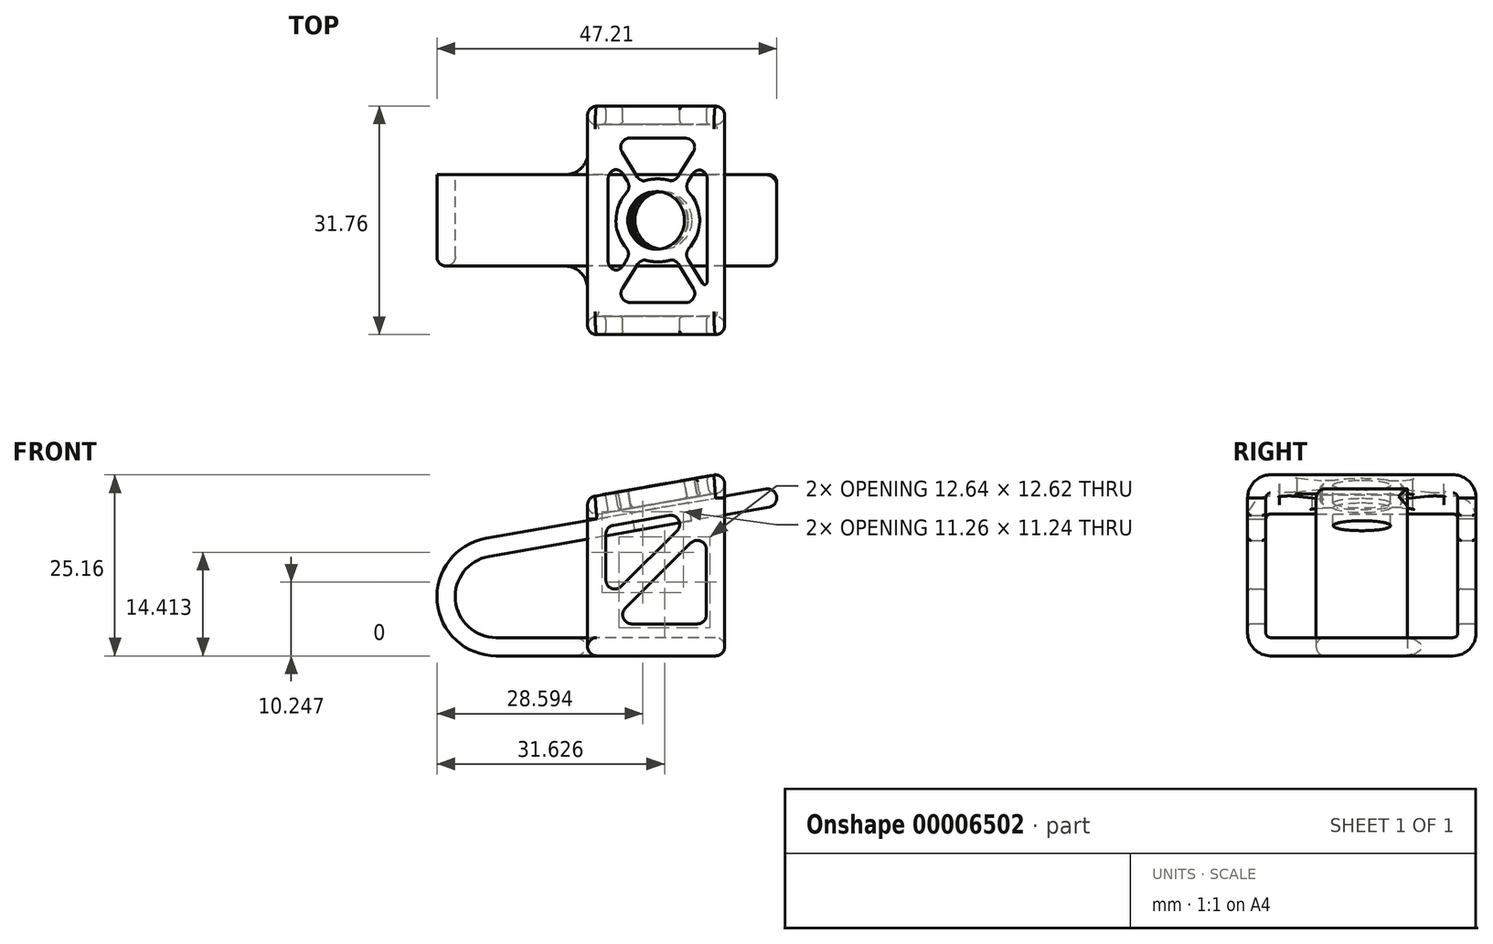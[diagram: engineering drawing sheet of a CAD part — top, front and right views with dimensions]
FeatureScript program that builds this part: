
annotation { "Feature Type Name" : "Feature", "Feature Type Description" : "" }
export const myFeature = defineFeature(function(context is Context, id is Id, definition is map)
    precondition{}
    {
        {
            var Q0;
            Q0=qCreatedBy(makeId("Front.planeOp"),FACE);
            var sketch = newSketch(context, id + "F0", { "sketchPlane" : qUnion([Q0])});
            skLineSegment(sketch, "E0", {"start": v(0, 0) * mm, "end": v(0, 22.04) * mm});
            skLineSegment(sketch, "E1", {"start": v(0, 22.04) * mm, "end": v(19.05, 25.4) * mm});
            skLineSegment(sketch, "E2", {"start": v(19.05, 25.4) * mm, "end": v(19.05, 0) * mm});
            skLineSegment(sketch, "E3", {"start": v(19.05, 0) * mm, "end": v(0, 0) * mm});
            skLineSegment(sketch, "E4", {"start": v(-64.45, 7.45) * mm, "end": v(67.26, 30.68) * mm, "construction": true});
            skSolve(sketch);
        }
        {
            var Q0;
            Q0=makeQuery(id+"F0.imprint","IMPRINT",FACE,{"disambiguationData":[TD([[makeQuery(id+"F0.imprint","IMPRINT",EDGE,{"derivedFrom":sQuery(id+"F0.wireOp",EDGE,"E0")}),-1.0]])]});
            extrude(context, id + "F1", {"entities" : qUnion([Q0]), "endBound" : BoundingType.SYMMETRIC, "depth" : 31.75 * mm});
        }
        {
            var Q0;
            Q0=makeQuery(id+"F1.opExtrude","CAP_EDGE",EDGE,{"disambiguationData":[OSD([sQuery(id+"F0.wireOp",EDGE,"E1")])],"isStart":true});
            var Q1;
            Q1=makeQuery(id+"F1.opExtrude","CAP_EDGE",EDGE,{"disambiguationData":[OSD([sQuery(id+"F0.wireOp",EDGE,"E1")])],"isStart":false});
            var Q2;
            Q2=makeQuery(id+"F1.opExtrude","CAP_EDGE",EDGE,{"disambiguationData":[OSD([sQuery(id+"F0.wireOp",EDGE,"E3")])],"isStart":false});
            var Q3;
            Q3=makeQuery(id+"F1.opExtrude","CAP_EDGE",EDGE,{"disambiguationData":[OSD([sQuery(id+"F0.wireOp",EDGE,"E3")])],"isStart":true});
            fillet(context, id + "F2", {"entities" : qUnion([Q0, Q1, Q2, Q3]), "radius" : 3.17 * mm, "tangentPropagation" : true, "allowEdgeOverflow" : false});
        }
        {
            var Q0;
            Q0=makeQuery(id+"F1.opExtrude","SWEPT_FACE",FACE,{"disambiguationData":[OSD([sQuery(id+"F0.wireOp",EDGE,"E0")])]});
            var Q1;
            Q1=makeQuery(id+"F1.opExtrude","SWEPT_FACE",FACE,{"disambiguationData":[OSD([sQuery(id+"F0.wireOp",EDGE,"E2")])]});
            shell(context, id + "F3", {"entities" : qUnion([Q0, Q1]), "thickness" : 2.54 * mm});
        }
        {
            var Q0;
            Q0=qCreatedBy(makeId("Top.planeOp"),FACE);
            var sketch = newSketch(context, id + "F4", { "sketchPlane" : qUnion([Q0])});
            skLineSegment(sketch, "E5", {"start": v(0.07, 10.16) * mm, "end": v(5.08, 10.16) * mm});
            skLineSegment(sketch, "E6", {"start": v(0.07, 10.16) * mm, "end": v(0.07, 9.53) * mm});
            skLineSegment(sketch, "E7", {"start": v(-3.1, 6.35) * mm, "end": v(-12.7, 6.35) * mm});
            skPoint(sketch, "E8.visualSharp", {"position": v(0.07, 6.35) * mm});
            skArc(sketch, "E8.filletArc", {"start": v(-3.1, 6.35) * mm, "mid": v(-0.86, 7.28) * mm, "end": v(0.07, 9.53) * mm});
            skLineSegment(sketch, "E9", {"start": v(-12.7, 6.35) * mm, "end": v(-12.7, -6.35) * mm});
            skLineSegment(sketch, "E10", {"start": v(-12.7, -6.35) * mm, "end": v(-3.18, -6.35) * mm});
            skLineSegment(sketch, "E11", {"start": v(0, -9.52) * mm, "end": v(0, -10.16) * mm});
            skLineSegment(sketch, "E12", {"start": v(0, -10.16) * mm, "end": v(5.08, -10.16) * mm});
            skLineSegment(sketch, "E13", {"start": v(5.08, -10.16) * mm, "end": v(5.08, 10.16) * mm});
            skPoint(sketch, "E14.visualSharp", {"position": v(0, -6.35) * mm});
            skArc(sketch, "E14.filletArc", {"start": v(0, -9.52) * mm, "mid": v(-0.93, -7.28) * mm, "end": v(-3.18, -6.35) * mm});
            skLineSegment(sketch, "E15", {"start": v(-12.7, 0) * mm, "end": v(0, 0) * mm, "construction": true});
            skSolve(sketch);
        }
        {
            var Q0;
            Q0=makeQuery(id+"F4.imprint","IMPRINT",FACE,{"disambiguationData":[TD([[makeQuery(id+"F4.imprint","IMPRINT",EDGE,{"derivedFrom":sQuery(id+"F4.wireOp",EDGE,"E5")}),-1.0]])]});
            extrude(context, id + "F5", {"entities" : qUnion([Q0]), "operationType" : NewBodyOperationType.ADD, "depth" : 2.54 * mm});
        }
        {
            var Q0;
            Q0=makeQuery(id+"F1.opExtrude","CAP_FACE",FACE,{"disambiguationData":[OSD([sQuery(id+"F0.wireOp",EDGE,"E0"),sQuery(id+"F0.wireOp",EDGE,"E1"),sQuery(id+"F0.wireOp",EDGE,"E2"),sQuery(id+"F0.wireOp",EDGE,"E3")])],"isStart":false});
            var sketch = newSketch(context, id + "F6", { "sketchPlane" : qUnion([Q0])});
            skLineSegment(sketch, "E16", {"start": v(19.05, 22.18) * mm, "end": v(0, 3.18) * mm, "construction": true});
            skLineSegment(sketch, "E17", {"start": v(2.54, 7.5) * mm, "end": v(2.54, 17.98) * mm});
            skLineSegment(sketch, "E18", {"start": v(2.54, 17.98) * mm, "end": v(15.3, 20.22) * mm});
            skLineSegment(sketch, "E19", {"start": v(15.3, 20.22) * mm, "end": v(2.54, 7.5) * mm});
            skLineSegment(sketch, "E20", {"start": v(16.51, 17.85) * mm, "end": v(3.07, 4.45) * mm});
            skLineSegment(sketch, "E21", {"start": v(3.07, 4.45) * mm, "end": v(16.51, 4.45) * mm});
            skLineSegment(sketch, "E22", {"start": v(16.51, 4.45) * mm, "end": v(16.51, 17.85) * mm});
            skSolve(sketch);
        }
        {
            var Q0;
            Q0 = qSketchRegion(id + "F6", true);
            extrude(context, id + "F7", {"entities" : qUnion([Q0]), "operationType" : NewBodyOperationType.REMOVE, "endBound" : BoundingType.THROUGH_ALL, "oppositeDirection" : true, "depth" : 25.4 * mm});
        }
        {
            var Q0;
            Q0=qCreatedBy(makeId("Front.planeOp"),FACE);
            var sketch = newSketch(context, id + "F8", { "sketchPlane" : qUnion([Q0])});
            skLineSegment(sketch, "E23.0", {"start": v(-14.13, 16.33) * mm, "end": v(67.26, 30.68) * mm});
            skLineSegment(sketch, "E24", {"start": v(0, 0) * mm, "end": v(-12.7, 0) * mm});
            skArc(sketch, "E25", {"start": v(-12.7, 0) * mm, "mid": v(-20.9, 7.5) * mm, "end": v(-14.13, 16.33) * mm});
            skPoint(sketch, "E26.orphan", {"position": v(-64.45, 7.45) * mm});
            skLineSegment(sketch, "E27", {"start": v(0, 0) * mm, "end": v(0, 2.54) * mm});
            skLineSegment(sketch, "E28", {"start": v(0, 2.54) * mm, "end": v(-12.7, 2.54) * mm});
            skArc(sketch, "E29", {"start": v(-13.69, 13.82) * mm, "mid": v(-18.36, 7.73) * mm, "end": v(-12.7, 2.54) * mm});
            skLineSegment(sketch, "E30", {"start": v(26.04, 23.4) * mm, "end": v(26.48, 20.9) * mm});
            skLineSegment(sketch, "E31", {"start": v(26.48, 20.9) * mm, "end": v(-13.69, 13.82) * mm});
            skSolve(sketch);
        }
        {
            var Q0;
            Q0=makeQuery(id+"F8.imprint","IMPRINT",FACE,{"disambiguationData":[TD([[makeQuery(id+"F8.imprint","IMPRINT",EDGE,{"derivedFrom":sQuery(id+"F8.wireOp",EDGE,"E24")}),-1.0]])]});
            extrude(context, id + "F9", {"entities" : qUnion([Q0]), "operationType" : NewBodyOperationType.ADD, "endBound" : BoundingType.SYMMETRIC, "depth" : 12.7 * mm});
        }
        {
            var Q0;
            Q0=makeQuery(id+"F1.opExtrude","SWEPT_FACE",FACE,{"disambiguationData":[OSD([sQuery(id+"F0.wireOp",EDGE,"E1")])]});
            var sketch = newSketch(context, id + "F10", { "sketchPlane" : qUnion([Q0])});
            skLineSegment(sketch, "E32", {"start": v(3.83, 12.7) * mm, "end": v(23.17, -12.7) * mm, "construction": true});
            skCircle(sketch, "E33", {"center": v(13.5, 0) * mm, "radius": 4 * mm});
            skSolve(sketch);
        }
        {
            var Q0;
            Q0=makeQuery(id+"F10.imprint","IMPRINT",FACE,{"disambiguationData":[TD([[makeQuery(id+"F10.imprint","IMPRINT",EDGE,{"derivedFrom":sQuery(id+"F10.wireOp",EDGE,"E33")}),-1.0]])]});
            var sketch = newSketch(context, id + "F11", { "sketchPlane" : qUnion([Q0])});
            skArc(sketch, "E34", {"start": v(15.96, 5.22) * mm, "mid": v(13.48, 5.76) * mm, "end": v(11, 5.19) * mm});
            skLineSegment(sketch, "E35.0", {"start": v(20.63, -10.23) * mm, "end": v(20.63, 10.23) * mm});
            skLineSegment(sketch, "E35.2", {"start": v(6.37, -10.23) * mm, "end": v(6.37, 10.23) * mm});
            skLineSegment(sketch, "E35.3", {"start": v(7.12, 11.43) * mm, "end": v(19.88, 11.43) * mm});
            skLineSegment(sketch, "E36", {"start": v(19.88, -11.43) * mm, "end": v(7.12, -11.43) * mm});
            skLineSegment(sketch, "E37.0", {"start": v(19.88, 11.43) * mm, "end": v(15.96, 5.22) * mm});
            skLineSegment(sketch, "E38.0", {"start": v(20.63, 10.23) * mm, "end": v(17.1, 4.5) * mm});
            skLineSegment(sketch, "E39.0", {"start": v(20.63, -10.23) * mm, "end": v(17.08, -4.53) * mm});
            skLineSegment(sketch, "E40.0", {"start": v(19.88, -11.43) * mm, "end": v(16, -5.2) * mm});
            skLineSegment(sketch, "E41.trimOffspring", {"start": v(11, 5.19) * mm, "end": v(7.12, 11.43) * mm});
            skArc(sketch, "E42.trimOffspring", {"start": v(11.1, -5.23) * mm, "mid": v(13.55, -5.76) * mm, "end": v(16, -5.2) * mm});
            skLineSegment(sketch, "E43.trimOffspring", {"start": v(9.93, 4.51) * mm, "end": v(6.37, 10.23) * mm});
            skLineSegment(sketch, "E44.trimOffspring", {"start": v(9.85, -4.45) * mm, "end": v(6.37, -10.23) * mm});
            skLineSegment(sketch, "E45.trimOffspring", {"start": v(11.1, -5.23) * mm, "end": v(7.12, -11.43) * mm});
            skArc(sketch, "E46.trimOffspring", {"start": v(17.08, -4.53) * mm, "mid": v(19.28, -0.02) * mm, "end": v(17.1, 4.5) * mm});
            skArc(sketch, "E47.trimOffspring", {"start": v(9.93, 4.51) * mm, "mid": v(7.75, 0.05) * mm, "end": v(9.85, -4.45) * mm});
            skSolve(sketch);
        }
        {
            var Q0;
            Q0=makeQuery(id+"F10.imprint","IMPRINT",FACE,{"disambiguationData":[TD([[makeQuery(id+"F10.imprint","IMPRINT",EDGE,{"derivedFrom":sQuery(id+"F10.wireOp",EDGE,"E33")}),1.0]])]});
            extrude(context, id + "F12", {"entities" : qUnion([Q0]), "operationType" : NewBodyOperationType.REMOVE, "oppositeDirection" : true, "depth" : 12.7 * mm});
        }
        {
            var Q0;
            Q0=makeQuery(id+"F1.opExtrude","SWEPT_FACE",FACE,{"disambiguationData":[OSD([sQuery(id+"F0.wireOp",EDGE,"E0")])]});
            var Q1;
            Q1=makeQuery(id+"F5.opExtrude","SWEPT_FACE",FACE,{"disambiguationData":[OSD([sQuery(id+"F4.wireOp",EDGE,"E14.filletArc")])]});
            var Q2;
            Q2=makeQuery(id+"F9.boolean.opBoolean","MERGE",FACE,{"derivedFrom":[makeQuery(id+"F5.opExtrude","SWEPT_FACE",FACE,{"disambiguationData":[OSD([sQuery(id+"F4.wireOp",EDGE,"E10")])]}),makeQuery(id+"F9.opExtrude","CAP_FACE",FACE,{"disambiguationData":[OSD([sQuery(id+"F8.wireOp",EDGE,"E23.0"),sQuery(id+"F8.wireOp",EDGE,"E24"),sQuery(id+"F8.wireOp",EDGE,"E25"),sQuery(id+"F8.wireOp",EDGE,"E27"),sQuery(id+"F8.wireOp",EDGE,"E28"),sQuery(id+"F8.wireOp",EDGE,"E29"),sQuery(id+"F8.wireOp",EDGE,"E30"),sQuery(id+"F8.wireOp",EDGE,"E31")])],"isStart":false})]});
            var Q3;
            Q3=makeQuery(id+"F9.opExtrude","SWEPT_FACE",FACE,{"disambiguationData":[OSD([sQuery(id+"F8.wireOp",EDGE,"E30")])]});
            var Q4;
            Q4=makeQuery(id+"F1.opExtrude","SWEPT_FACE",FACE,{"disambiguationData":[OSD([sQuery(id+"F0.wireOp",EDGE,"E2")])]});
            fillet(context, id + "F13", {"entities" : qUnion([Q0, Q1, Q2, Q3, Q4]), "radius" : 1.27 * mm, "tangentPropagation" : true, "allowEdgeOverflow" : false});
        }
        {
            var Q0;
            Q0=makeQuery(id+"F11.imprint","IMPRINT",FACE,{"disambiguationData":[TD([[makeQuery(id+"F11.imprint","IMPRINT",EDGE,{"derivedFrom":sQuery(id+"F11.wireOp",EDGE,"E34")}),-1.0]])]});
            var Q1;
            Q1=makeQuery(id+"F11.imprint","IMPRINT",FACE,{"disambiguationData":[TD([[makeQuery(id+"F11.imprint","IMPRINT",EDGE,{"derivedFrom":sQuery(id+"F11.wireOp",EDGE,"E35.0")}),1.0]])]});
            var Q2;
            Q2=makeQuery(id+"F11.imprint","IMPRINT",FACE,{"disambiguationData":[TD([[makeQuery(id+"F11.imprint","IMPRINT",EDGE,{"derivedFrom":sQuery(id+"F11.wireOp",EDGE,"E36")}),-1.0]])]});
            var Q3;
            Q3=makeQuery(id+"F11.imprint","IMPRINT",FACE,{"disambiguationData":[TD([[makeQuery(id+"F11.imprint","IMPRINT",EDGE,{"derivedFrom":sQuery(id+"F11.wireOp",EDGE,"E35.2")}),-1.0]])]});
            extrude(context, id + "F14", {"entities" : qUnion([Q0, Q1, Q2, Q3]), "operationType" : NewBodyOperationType.REMOVE, "oppositeDirection" : true, "depth" : 2.54 * mm});
        }
        {
            var Q0;
            Q0=makeQuery(id+"F14.boolean.opBoolean","COPY",EDGE,{"derivedFrom":makeQuery(id+"F14.opExtrude","SWEPT_EDGE",EDGE,{"disambiguationData":[OSD([sQuery(id+"F11.wireOp",EDGE,"E35.3"),sQuery(id+"F11.wireOp",EDGE,"E41.trimOffspring")])]})});
            var Q1;
            Q1=makeQuery(id+"F14.boolean.opBoolean","COPY",EDGE,{"derivedFrom":makeQuery(id+"F14.opExtrude","SWEPT_EDGE",EDGE,{"disambiguationData":[OSD([sQuery(id+"F11.wireOp",EDGE,"E35.2"),sQuery(id+"F11.wireOp",EDGE,"E43.trimOffspring")])]})});
            var Q2;
            Q2=makeQuery(id+"F14.boolean.opBoolean","COPY",EDGE,{"derivedFrom":makeQuery(id+"F14.opExtrude","SWEPT_EDGE",EDGE,{"disambiguationData":[OSD([sQuery(id+"F11.wireOp",EDGE,"E43.trimOffspring"),sQuery(id+"F11.wireOp",EDGE,"E47.trimOffspring")])]})});
            var Q3;
            Q3=makeQuery(id+"F14.boolean.opBoolean","COPY",EDGE,{"derivedFrom":makeQuery(id+"F14.opExtrude","SWEPT_EDGE",EDGE,{"disambiguationData":[OSD([sQuery(id+"F11.wireOp",EDGE,"E44.trimOffspring"),sQuery(id+"F11.wireOp",EDGE,"E47.trimOffspring")])]})});
            var Q4;
            Q4=makeQuery(id+"F14.boolean.opBoolean","COPY",EDGE,{"derivedFrom":makeQuery(id+"F14.opExtrude","SWEPT_EDGE",EDGE,{"disambiguationData":[OSD([sQuery(id+"F11.wireOp",EDGE,"E35.2"),sQuery(id+"F11.wireOp",EDGE,"E44.trimOffspring")])]})});
            var Q5;
            Q5=makeQuery(id+"F14.boolean.opBoolean","COPY",EDGE,{"derivedFrom":makeQuery(id+"F14.opExtrude","SWEPT_EDGE",EDGE,{"disambiguationData":[OSD([sQuery(id+"F11.wireOp",EDGE,"E36"),sQuery(id+"F11.wireOp",EDGE,"E45.trimOffspring")])]})});
            var Q6;
            Q6=makeQuery(id+"F14.boolean.opBoolean","COPY",EDGE,{"derivedFrom":makeQuery(id+"F14.opExtrude","SWEPT_EDGE",EDGE,{"disambiguationData":[OSD([sQuery(id+"F11.wireOp",EDGE,"E42.trimOffspring"),sQuery(id+"F11.wireOp",EDGE,"E45.trimOffspring")])]})});
            var Q7;
            Q7=makeQuery(id+"F14.boolean.opBoolean","COPY",EDGE,{"derivedFrom":makeQuery(id+"F14.opExtrude","SWEPT_EDGE",EDGE,{"disambiguationData":[OSD([sQuery(id+"F11.wireOp",EDGE,"E40.0"),sQuery(id+"F11.wireOp",EDGE,"E42.trimOffspring")])]})});
            var Q8;
            Q8=makeQuery(id+"F14.boolean.opBoolean","COPY",EDGE,{"derivedFrom":makeQuery(id+"F14.opExtrude","SWEPT_EDGE",EDGE,{"disambiguationData":[OSD([sQuery(id+"F11.wireOp",EDGE,"E36"),sQuery(id+"F11.wireOp",EDGE,"E40.0")])]})});
            var Q9;
            Q9=makeQuery(id+"F14.boolean.opBoolean","COPY",EDGE,{"derivedFrom":makeQuery(id+"F14.opExtrude","SWEPT_EDGE",EDGE,{"disambiguationData":[OSD([sQuery(id+"F11.wireOp",EDGE,"E34"),sQuery(id+"F11.wireOp",EDGE,"E37.0")])]})});
            var Q10;
            Q10=makeQuery(id+"F14.boolean.opBoolean","COPY",EDGE,{"derivedFrom":makeQuery(id+"F14.opExtrude","SWEPT_EDGE",EDGE,{"disambiguationData":[OSD([sQuery(id+"F11.wireOp",EDGE,"E34"),sQuery(id+"F11.wireOp",EDGE,"E41.trimOffspring")])]})});
            var Q11;
            Q11=makeQuery(id+"F14.boolean.opBoolean","COPY",EDGE,{"derivedFrom":makeQuery(id+"F14.opExtrude","SWEPT_EDGE",EDGE,{"disambiguationData":[OSD([sQuery(id+"F11.wireOp",EDGE,"E39.0"),sQuery(id+"F11.wireOp",EDGE,"E46.trimOffspring")])]})});
            var Q12;
            Q12=makeQuery(id+"F14.boolean.opBoolean","COPY",EDGE,{"derivedFrom":makeQuery(id+"F14.opExtrude","SWEPT_EDGE",EDGE,{"disambiguationData":[OSD([sQuery(id+"F11.wireOp",EDGE,"E38.0"),sQuery(id+"F11.wireOp",EDGE,"E46.trimOffspring")])]})});
            var Q13;
            Q13=makeQuery(id+"F14.boolean.opBoolean","COPY",EDGE,{"derivedFrom":makeQuery(id+"F14.opExtrude","SWEPT_EDGE",EDGE,{"disambiguationData":[OSD([sQuery(id+"F11.wireOp",EDGE,"E35.3"),sQuery(id+"F11.wireOp",EDGE,"E37.0")])]})});
            var Q14;
            Q14=makeQuery(id+"F14.boolean.opBoolean","COPY",EDGE,{"derivedFrom":makeQuery(id+"F14.opExtrude","SWEPT_EDGE",EDGE,{"disambiguationData":[OSD([sQuery(id+"F11.wireOp",EDGE,"E35.0"),sQuery(id+"F11.wireOp",EDGE,"E38.0")])]})});
            fillet(context, id + "F15", {"entities" : qUnion([Q0, Q1, Q2, Q3, Q4, Q5, Q6, Q7, Q8, Q9, Q10, Q11, Q12, Q13, Q14]), "radius" : 1.27 * mm, "tangentPropagation" : true, "allowEdgeOverflow" : false});
        }
        {
            var Q0;
            Q0=makeQuery(id+"F14.boolean.opBoolean","COPY",FACE,{"derivedFrom":makeQuery(id+"F14.opExtrude","SWEPT_FACE",FACE,{"disambiguationData":[OSD([sQuery(id+"F11.wireOp",EDGE,"E37.0")])]})});
            var Q1;
            Q1=makeQuery(id+"F14.boolean.opBoolean","COPY",FACE,{"derivedFrom":makeQuery(id+"F14.opExtrude","SWEPT_FACE",FACE,{"disambiguationData":[OSD([sQuery(id+"F11.wireOp",EDGE,"E35.0")])]})});
            var Q2;
            Q2=makeQuery(id+"F15.opFillet","BLEND_FACE",FACE,{"disambiguationData":[OSD([sQuery(id+"F11.wireOp",EDGE,"E36"),sQuery(id+"F11.wireOp",EDGE,"E40.0")])]});
            var Q3;
            Q3=makeQuery(id+"F14.boolean.opBoolean","COPY",FACE,{"derivedFrom":makeQuery(id+"F14.opExtrude","SWEPT_FACE",FACE,{"disambiguationData":[OSD([sQuery(id+"F11.wireOp",EDGE,"E44.trimOffspring")])]})});
            fillet(context, id + "F16", {"entities" : qUnion([Q0, Q1, Q2, Q3]), "radius" : 0.5 * mm, "tangentPropagation" : true, "allowEdgeOverflow" : false});
        }
        {
            var Q0;
            Q0=makeQuery(id+"F7.boolean.opBoolean","COPY",EDGE,{"disambiguationData":[OD(1.0)],"derivedFrom":makeQuery(id+"F7.opExtrude","SWEPT_EDGE",EDGE,{"disambiguationData":[OSD([sQuery(id+"F6.wireOp",EDGE,"E17"),sQuery(id+"F6.wireOp",EDGE,"E18")])]})});
            var Q1;
            Q1=makeQuery(id+"F7.boolean.opBoolean","COPY",EDGE,{"disambiguationData":[OD(1.0)],"derivedFrom":makeQuery(id+"F7.opExtrude","SWEPT_EDGE",EDGE,{"disambiguationData":[OSD([sQuery(id+"F6.wireOp",EDGE,"E18"),sQuery(id+"F6.wireOp",EDGE,"E19")])]})});
            var Q2;
            Q2=makeQuery(id+"F7.boolean.opBoolean","COPY",EDGE,{"disambiguationData":[OD(1.0)],"derivedFrom":makeQuery(id+"F7.opExtrude","SWEPT_EDGE",EDGE,{"disambiguationData":[OSD([sQuery(id+"F6.wireOp",EDGE,"E17"),sQuery(id+"F6.wireOp",EDGE,"E19")])]})});
            var Q3;
            Q3=makeQuery(id+"F7.boolean.opBoolean","COPY",EDGE,{"disambiguationData":[OD(1.0)],"derivedFrom":makeQuery(id+"F7.opExtrude","SWEPT_EDGE",EDGE,{"disambiguationData":[OSD([sQuery(id+"F6.wireOp",EDGE,"E21"),sQuery(id+"F6.wireOp",EDGE,"E22")])]})});
            var Q4;
            Q4=makeQuery(id+"F7.boolean.opBoolean","COPY",EDGE,{"disambiguationData":[OD(0.0)],"derivedFrom":makeQuery(id+"F7.opExtrude","SWEPT_EDGE",EDGE,{"disambiguationData":[OSD([sQuery(id+"F6.wireOp",EDGE,"E21"),sQuery(id+"F6.wireOp",EDGE,"E22")])]})});
            var Q5;
            Q5=makeQuery(id+"F7.boolean.opBoolean","COPY",EDGE,{"disambiguationData":[OD(1.0)],"derivedFrom":makeQuery(id+"F7.opExtrude","SWEPT_EDGE",EDGE,{"disambiguationData":[OSD([sQuery(id+"F6.wireOp",EDGE,"E20"),sQuery(id+"F6.wireOp",EDGE,"E21")])]})});
            var Q6;
            Q6=makeQuery(id+"F7.boolean.opBoolean","COPY",EDGE,{"disambiguationData":[OD(1.0)],"derivedFrom":makeQuery(id+"F7.opExtrude","SWEPT_EDGE",EDGE,{"disambiguationData":[OSD([sQuery(id+"F6.wireOp",EDGE,"E20"),sQuery(id+"F6.wireOp",EDGE,"E22")])]})});
            var Q7;
            Q7=makeQuery(id+"F7.boolean.opBoolean","COPY",EDGE,{"disambiguationData":[OD(0.0)],"derivedFrom":makeQuery(id+"F7.opExtrude","SWEPT_EDGE",EDGE,{"disambiguationData":[OSD([sQuery(id+"F6.wireOp",EDGE,"E17"),sQuery(id+"F6.wireOp",EDGE,"E18")])]})});
            var Q8;
            Q8=makeQuery(id+"F7.boolean.opBoolean","COPY",EDGE,{"disambiguationData":[OD(0.0)],"derivedFrom":makeQuery(id+"F7.opExtrude","SWEPT_EDGE",EDGE,{"disambiguationData":[OSD([sQuery(id+"F6.wireOp",EDGE,"E18"),sQuery(id+"F6.wireOp",EDGE,"E19")])]})});
            var Q9;
            Q9=makeQuery(id+"F7.boolean.opBoolean","COPY",EDGE,{"disambiguationData":[OD(0.0)],"derivedFrom":makeQuery(id+"F7.opExtrude","SWEPT_EDGE",EDGE,{"disambiguationData":[OSD([sQuery(id+"F6.wireOp",EDGE,"E20"),sQuery(id+"F6.wireOp",EDGE,"E22")])]})});
            var Q10;
            Q10=makeQuery(id+"F7.boolean.opBoolean","COPY",EDGE,{"disambiguationData":[OD(0.0)],"derivedFrom":makeQuery(id+"F7.opExtrude","SWEPT_EDGE",EDGE,{"disambiguationData":[OSD([sQuery(id+"F6.wireOp",EDGE,"E20"),sQuery(id+"F6.wireOp",EDGE,"E21")])]})});
            var Q11;
            Q11=makeQuery(id+"F7.boolean.opBoolean","COPY",EDGE,{"disambiguationData":[OD(0.0)],"derivedFrom":makeQuery(id+"F7.opExtrude","SWEPT_EDGE",EDGE,{"disambiguationData":[OSD([sQuery(id+"F6.wireOp",EDGE,"E17"),sQuery(id+"F6.wireOp",EDGE,"E19")])]})});
            fillet(context, id + "F17", {"entities" : qUnion([Q0, Q1, Q2, Q3, Q4, Q5, Q6, Q7, Q8, Q9, Q10, Q11]), "radius" : 1.27 * mm, "tangentPropagation" : true, "allowEdgeOverflow" : false});
        }
        {
            var Q0;
            Q0=makeQuery(id+"F7.boolean.opBoolean","COPY",FACE,{"disambiguationData":[OD(0.0)],"derivedFrom":makeQuery(id+"F7.opExtrude","SWEPT_FACE",FACE,{"disambiguationData":[OSD([sQuery(id+"F6.wireOp",EDGE,"E18")])]})});
            var Q1;
            {var subQ0=sQuery(id+"F6.wireOp",EDGE,"E20");var subQ1=sQuery(id+"F6.wireOp",EDGE,"E22");Q1=makeQuery(id+"F17.opFillet","BLEND_FACE",FACE,{"disambiguationData":[OSD([subQ0,subQ1]),TDD([makeQuery(id+"F7.boolean.opBoolean","COPY",EDGE,{"disambiguationData":[OD(0.0)],"derivedFrom":makeQuery(id+"F7.opExtrude","SWEPT_EDGE",EDGE,{"disambiguationData":[OSD([subQ0,subQ1])]})})])]});}
            var Q2;
            Q2=makeQuery(id+"F7.boolean.opBoolean","COPY",FACE,{"disambiguationData":[OD(1.0)],"derivedFrom":makeQuery(id+"F7.opExtrude","SWEPT_FACE",FACE,{"disambiguationData":[OSD([sQuery(id+"F6.wireOp",EDGE,"E17")])]})});
            var Q3;
            Q3=makeQuery(id+"F7.boolean.opBoolean","COPY",FACE,{"disambiguationData":[OD(1.0)],"derivedFrom":makeQuery(id+"F7.opExtrude","SWEPT_FACE",FACE,{"disambiguationData":[OSD([sQuery(id+"F6.wireOp",EDGE,"E20")])]})});
            fillet(context, id + "F18", {"entities" : qUnion([Q0, Q1, Q2, Q3]), "radius" : 0.5 * mm, "tangentPropagation" : true, "allowEdgeOverflow" : false});
        }
    });
